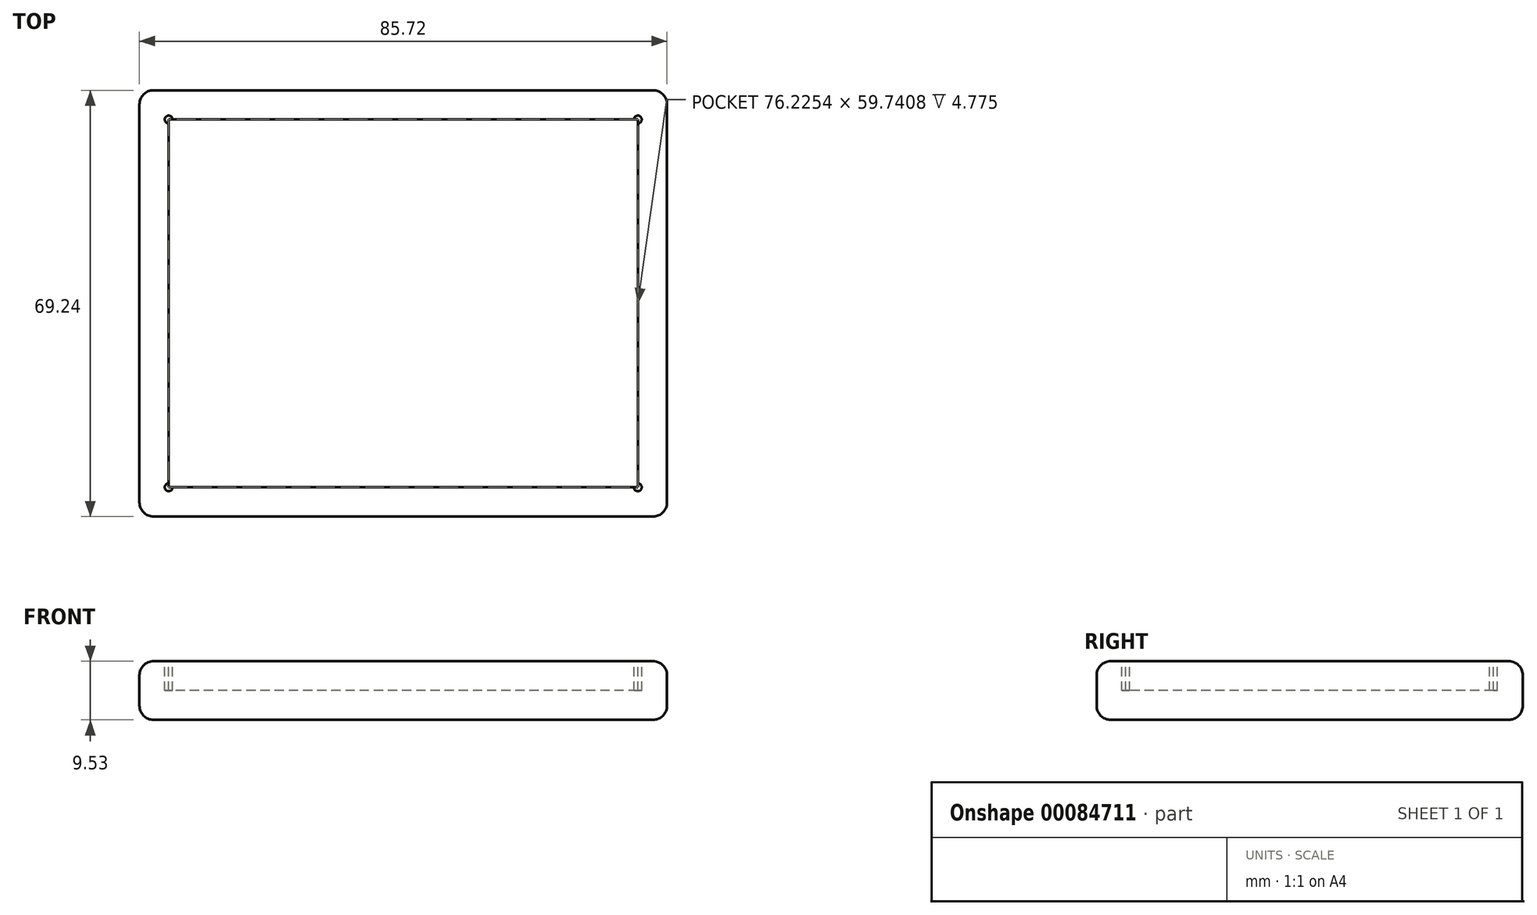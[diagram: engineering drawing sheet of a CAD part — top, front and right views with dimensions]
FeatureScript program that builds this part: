
annotation { "Feature Type Name" : "Feature", "Feature Type Description" : "" }
export const myFeature = defineFeature(function(context is Context, id is Id, definition is map)
    precondition{}
    {
        {
            var Q0;
            Q0=qCreatedBy(makeId("Top.planeOp"),FACE);
            var sketch = newSketch(context, id + "F0", { "sketchPlane" : qUnion([Q0])});
            skLineSegment(sketch, "E0.rect.bottom", {"start": v(42.86, 34.62) * mm, "end": v(-42.86, 34.62) * mm});
            skLineSegment(sketch, "E0.rect.top", {"start": v(42.86, -34.62) * mm, "end": v(-42.86, -34.62) * mm});
            skLineSegment(sketch, "E0.rect.left", {"start": v(42.86, 34.62) * mm, "end": v(42.86, -34.62) * mm});
            skLineSegment(sketch, "E0.rect.right", {"start": v(-42.86, 34.62) * mm, "end": v(-42.86, -34.62) * mm});
            skPoint(sketch, "E0.rect.middle", {"position": v(0, 0) * mm});
            skSolve(sketch);
        }
        {
            var Q0;
            Q0=qSketchRegion(id+"F0",true);
            extrude(context, id + "F1", {"entities" : qUnion([Q0]), "depth" : 9.52 * mm});
        }
        {
            var Q0;
            Q0=makeQuery(id+"F1.opExtrude","CAP_FACE",FACE,{"disambiguationData":[OSD([sQuery(id+"F0.wireOp",EDGE,"E0.rect.bottom"),sQuery(id+"F0.wireOp",EDGE,"E0.rect.top"),sQuery(id+"F0.wireOp",EDGE,"E0.rect.left"),sQuery(id+"F0.wireOp",EDGE,"E0.rect.right")])],"isStart":false});
            shell(context, id + "F2", {"entities" : qUnion([Q0]), "thickness" : 4.75 * mm});
        }
        {
            var Q0;
            Q0=makeQuery(id+"F1.opExtrude","CAP_FACE",FACE,{"disambiguationData":[OSD([sQuery(id+"F0.wireOp",EDGE,"E0.rect.bottom"),sQuery(id+"F0.wireOp",EDGE,"E0.rect.top"),sQuery(id+"F0.wireOp",EDGE,"E0.rect.left"),sQuery(id+"F0.wireOp",EDGE,"E0.rect.right")])],"isStart":false});
            var sketch = newSketch(context, id + "F3", { "sketchPlane" : qUnion([Q0])});
            skCircle(sketch, "E1", {"center": v(-38.11, 29.87) * mm, "radius": 0.64 * mm});
            skCircle(sketch, "E2", {"center": v(38.11, 29.87) * mm, "radius": 0.64 * mm});
            skCircle(sketch, "E3", {"center": v(38.11, -29.87) * mm, "radius": 0.64 * mm});
            skCircle(sketch, "E4", {"center": v(-38.11, -29.87) * mm, "radius": 0.64 * mm});
            skSolve(sketch);
        }
        {
            var Q0;
            Q0=qSketchRegion(id+"F3",true);
            extrude(context, id + "F4", {"entities" : qUnion([Q0]), "operationType" : NewBodyOperationType.REMOVE, "oppositeDirection" : true, "depth" : 4.76 * mm});
        }
        {
            var Q0;
            Q0=makeQuery(id+"F1.opExtrude","CAP_EDGE",EDGE,{"disambiguationData":[OSD([sQuery(id+"F0.wireOp",EDGE,"E0.rect.top")])],"isStart":false});
            var Q1;
            Q1=makeQuery(id+"F1.opExtrude","SWEPT_EDGE",EDGE,{"disambiguationData":[OSD([sQuery(id+"F0.wireOp",EDGE,"E0.rect.top"),sQuery(id+"F0.wireOp",EDGE,"E0.rect.right")])]});
            var Q2;
            Q2=makeQuery(id+"F1.opExtrude","CAP_EDGE",EDGE,{"disambiguationData":[OSD([sQuery(id+"F0.wireOp",EDGE,"E0.rect.right")])],"isStart":true});
            var Q3;
            Q3=makeQuery(id+"F1.opExtrude","CAP_EDGE",EDGE,{"disambiguationData":[OSD([sQuery(id+"F0.wireOp",EDGE,"E0.rect.right")])],"isStart":false});
            var Q4;
            Q4=makeQuery(id+"F1.opExtrude","CAP_EDGE",EDGE,{"disambiguationData":[OSD([sQuery(id+"F0.wireOp",EDGE,"E0.rect.top")])],"isStart":true});
            var Q5;
            Q5=makeQuery(id+"F1.opExtrude","SWEPT_EDGE",EDGE,{"disambiguationData":[OSD([sQuery(id+"F0.wireOp",EDGE,"E0.rect.top"),sQuery(id+"F0.wireOp",EDGE,"E0.rect.left")])]});
            var Q6;
            Q6=makeQuery(id+"F1.opExtrude","SWEPT_EDGE",EDGE,{"disambiguationData":[OSD([sQuery(id+"F0.wireOp",EDGE,"E0.rect.bottom"),sQuery(id+"F0.wireOp",EDGE,"E0.rect.right")])]});
            var Q7;
            Q7=makeQuery(id+"F1.opExtrude","CAP_EDGE",EDGE,{"disambiguationData":[OSD([sQuery(id+"F0.wireOp",EDGE,"E0.rect.bottom")])],"isStart":false});
            var Q8;
            Q8=makeQuery(id+"F1.opExtrude","CAP_EDGE",EDGE,{"disambiguationData":[OSD([sQuery(id+"F0.wireOp",EDGE,"E0.rect.bottom")])],"isStart":true});
            var Q9;
            Q9=makeQuery(id+"F1.opExtrude","SWEPT_EDGE",EDGE,{"disambiguationData":[OSD([sQuery(id+"F0.wireOp",EDGE,"E0.rect.bottom"),sQuery(id+"F0.wireOp",EDGE,"E0.rect.left")])]});
            var Q10;
            Q10=makeQuery(id+"F1.opExtrude","CAP_EDGE",EDGE,{"disambiguationData":[OSD([sQuery(id+"F0.wireOp",EDGE,"E0.rect.left")])],"isStart":false});
            var Q11;
            Q11=makeQuery(id+"F1.opExtrude","CAP_EDGE",EDGE,{"disambiguationData":[OSD([sQuery(id+"F0.wireOp",EDGE,"E0.rect.left")])],"isStart":true});
            fillet(context, id + "F5", {"entities" : qUnion([Q0, Q1, Q2, Q3, Q4, Q5, Q6, Q7, Q8, Q9, Q10, Q11]), "radius" : 2.3 * mm, "tangentPropagation" : true, "allowEdgeOverflow" : false});
        }
    });
